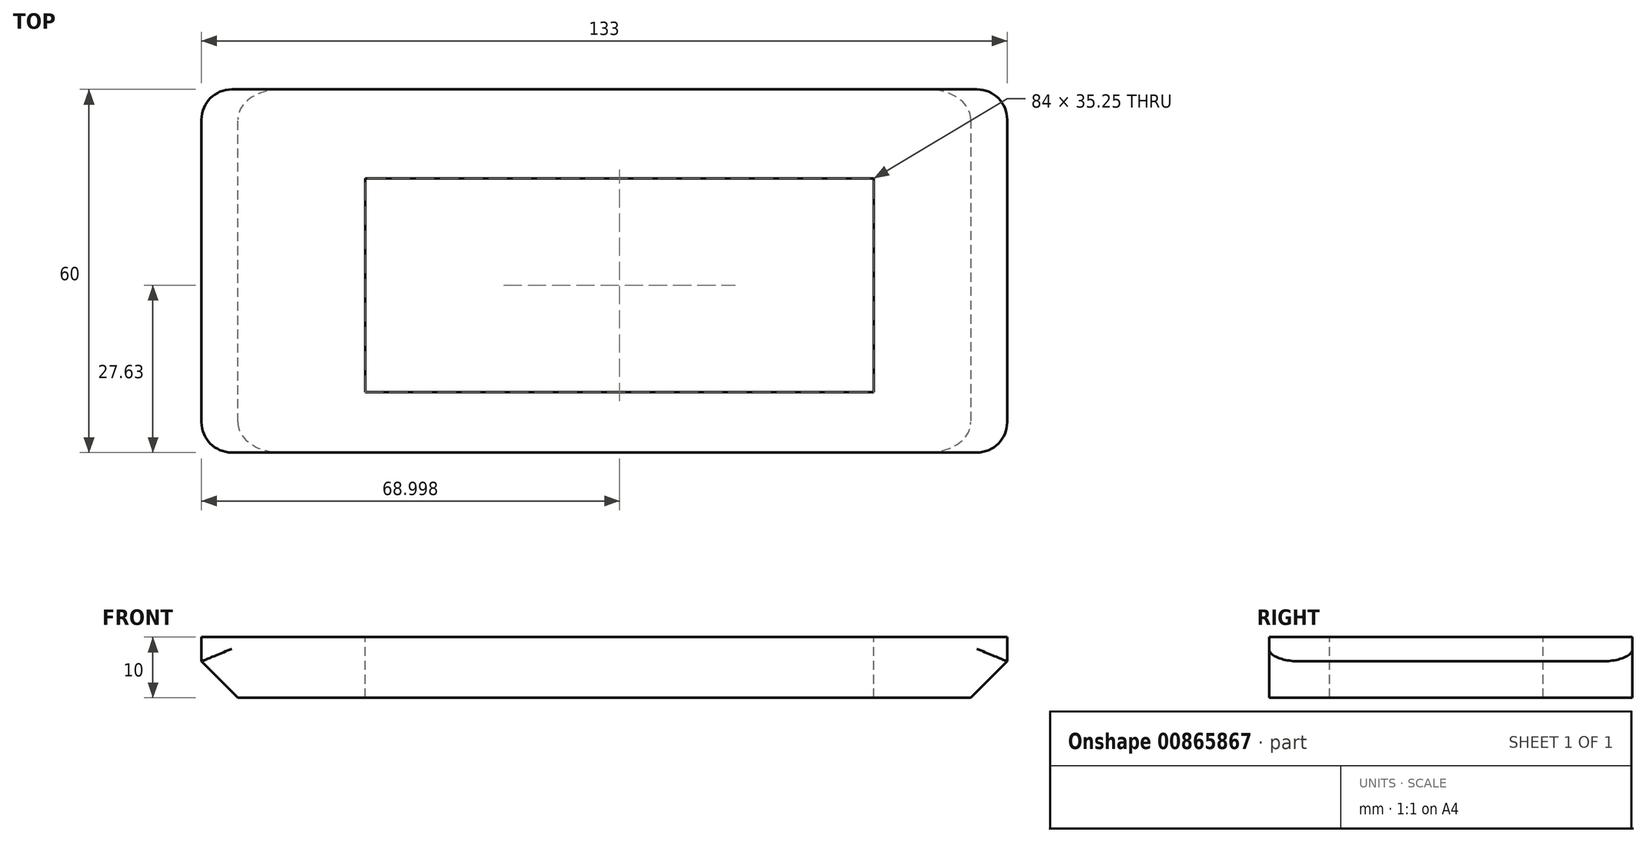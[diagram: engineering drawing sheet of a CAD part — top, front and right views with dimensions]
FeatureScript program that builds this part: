
annotation { "Feature Type Name" : "Feature", "Feature Type Description" : "" }
export const myFeature = defineFeature(function(context is Context, id is Id, definition is map)
    precondition{}
    {
        {
            var Q0;
            Q0=qCreatedBy(makeId("Top.planeOp"),FACE);
            var sketch = newSketch(context, id + "F0", { "sketchPlane" : qUnion([Q0])});
            skLineSegment(sketch, "E0.bottom", {"start": v(-68.33, 24.64) * mm, "end": v(64.67, 24.64) * mm});
            skLineSegment(sketch, "E0.top", {"start": v(-68.33, -35.36) * mm, "end": v(64.67, -35.36) * mm});
            skLineSegment(sketch, "E0.left", {"start": v(-68.33, 24.64) * mm, "end": v(-68.33, -35.36) * mm});
            skLineSegment(sketch, "E0.right", {"start": v(64.67, 24.64) * mm, "end": v(64.67, -35.36) * mm});
            skSolve(sketch);
        }
        {
            var Q0;
            Q0 = qSketchRegion(id + "F0", true);
            extrude(context, id + "F1", {"entities" : qUnion([Q0]), "depth" : 10 * mm, "offsetDistance" : 25 * mm});
        }
        {
            var Q0;
            Q0=makeQuery(id+"F1.opExtrude","CAP_FACE",FACE,{"disambiguationData":[OSD([sQuery(id+"F0.wireOp",EDGE,"E0.bottom"),sQuery(id+"F0.wireOp",EDGE,"E0.top"),sQuery(id+"F0.wireOp",EDGE,"E0.left"),sQuery(id+"F0.wireOp",EDGE,"E0.right")])],"isStart":false});
            var sketch = newSketch(context, id + "F2", { "sketchPlane" : qUnion([Q0])});
            skLineSegment(sketch, "E1.bottom", {"start": v(-41.33, 9.9) * mm, "end": v(42.67, 9.9) * mm});
            skLineSegment(sketch, "E1.top", {"start": v(-41.33, -25.36) * mm, "end": v(42.67, -25.36) * mm});
            skLineSegment(sketch, "E1.left", {"start": v(-41.33, 9.9) * mm, "end": v(-41.33, -25.36) * mm});
            skLineSegment(sketch, "E1.right", {"start": v(42.67, 9.9) * mm, "end": v(42.67, -25.36) * mm});
            skSolve(sketch);
        }
        {
            var Q0;
            Q0 = qSketchRegion(id + "F2", true);
            extrude(context, id + "F3", {"entities" : qUnion([Q0]), "operationType" : NewBodyOperationType.REMOVE, "endBound" : BoundingType.THROUGH_ALL, "oppositeDirection" : true, "depth" : 25 * mm, "offsetDistance" : 25 * mm});
        }
        {
            var Q0;
            Q0=makeQuery(id+"F1.opExtrude","CAP_EDGE",EDGE,{"disambiguationData":[OSD([sQuery(id+"F0.wireOp",EDGE,"E0.right")])],"isStart":true});
            var Q1;
            Q1=makeQuery(id+"F1.opExtrude","CAP_EDGE",EDGE,{"disambiguationData":[OSD([sQuery(id+"F0.wireOp",EDGE,"E0.left")])],"isStart":true});
            chamfer(context, id + "F4", {"entities" : qUnion([Q0, Q1]), "width" : 6 * mm, "tangentPropagation" : true});
        }
        {
            var Q0;
            Q0=makeQuery(id+"F1.opExtrude","SWEPT_EDGE",EDGE,{"disambiguationData":[OSD([sQuery(id+"F0.wireOp",EDGE,"E0.top"),sQuery(id+"F0.wireOp",EDGE,"E0.left")])]});
            var Q1;
            Q1=makeQuery(id+"F4.opChamfer","BLEND_EDGE",EDGE,{"blendedFrom":[makeQuery(id+"F1.opExtrude","CAP_EDGE",EDGE,{"disambiguationData":[OSD([sQuery(id+"F0.wireOp",EDGE,"E0.left")])],"isStart":true}),makeQuery(id+"F1.opExtrude","SWEPT_FACE",FACE,{"disambiguationData":[OSD([sQuery(id+"F0.wireOp",EDGE,"E0.top")])]})],"blendedInto":[makeQuery(id+"F1.opExtrude","SWEPT_FACE",FACE,{"disambiguationData":[OSD([sQuery(id+"F0.wireOp",EDGE,"E0.top")])]})]});
            var Q2;
            Q2=makeQuery(id+"F1.opExtrude","SWEPT_EDGE",EDGE,{"disambiguationData":[OSD([sQuery(id+"F0.wireOp",EDGE,"E0.bottom"),sQuery(id+"F0.wireOp",EDGE,"E0.left")])]});
            var Q3;
            Q3=makeQuery(id+"F4.opChamfer","BLEND_EDGE",EDGE,{"blendedFrom":[makeQuery(id+"F1.opExtrude","CAP_EDGE",EDGE,{"disambiguationData":[OSD([sQuery(id+"F0.wireOp",EDGE,"E0.left")])],"isStart":true}),makeQuery(id+"F1.opExtrude","SWEPT_FACE",FACE,{"disambiguationData":[OSD([sQuery(id+"F0.wireOp",EDGE,"E0.bottom")])]})],"blendedInto":[makeQuery(id+"F1.opExtrude","SWEPT_FACE",FACE,{"disambiguationData":[OSD([sQuery(id+"F0.wireOp",EDGE,"E0.bottom")])]})]});
            var Q4;
            Q4=makeQuery(id+"F1.opExtrude","SWEPT_EDGE",EDGE,{"disambiguationData":[OSD([sQuery(id+"F0.wireOp",EDGE,"E0.bottom"),sQuery(id+"F0.wireOp",EDGE,"E0.right")])]});
            var Q5;
            Q5=makeQuery(id+"F4.opChamfer","BLEND_EDGE",EDGE,{"blendedFrom":[makeQuery(id+"F1.opExtrude","CAP_EDGE",EDGE,{"disambiguationData":[OSD([sQuery(id+"F0.wireOp",EDGE,"E0.right")])],"isStart":true}),makeQuery(id+"F1.opExtrude","SWEPT_FACE",FACE,{"disambiguationData":[OSD([sQuery(id+"F0.wireOp",EDGE,"E0.bottom")])]})],"blendedInto":[makeQuery(id+"F1.opExtrude","SWEPT_FACE",FACE,{"disambiguationData":[OSD([sQuery(id+"F0.wireOp",EDGE,"E0.bottom")])]})]});
            var Q6;
            Q6=makeQuery(id+"F1.opExtrude","SWEPT_EDGE",EDGE,{"disambiguationData":[OSD([sQuery(id+"F0.wireOp",EDGE,"E0.top"),sQuery(id+"F0.wireOp",EDGE,"E0.right")])]});
            var Q7;
            Q7=makeQuery(id+"F4.opChamfer","BLEND_EDGE",EDGE,{"blendedFrom":[makeQuery(id+"F1.opExtrude","CAP_EDGE",EDGE,{"disambiguationData":[OSD([sQuery(id+"F0.wireOp",EDGE,"E0.right")])],"isStart":true}),makeQuery(id+"F1.opExtrude","SWEPT_FACE",FACE,{"disambiguationData":[OSD([sQuery(id+"F0.wireOp",EDGE,"E0.top")])]})],"blendedInto":[makeQuery(id+"F1.opExtrude","SWEPT_FACE",FACE,{"disambiguationData":[OSD([sQuery(id+"F0.wireOp",EDGE,"E0.top")])]})]});
            fillet(context, id + "F5", {"entities" : qUnion([Q0, Q1, Q2, Q3, Q4, Q5, Q6, Q7]), "tangentPropagation" : true, "radius" : 5 * mm, "defaultsChanged" : false, "vertexSettings" : [], "allowEdgeOverflow" : false});
        }
    });
